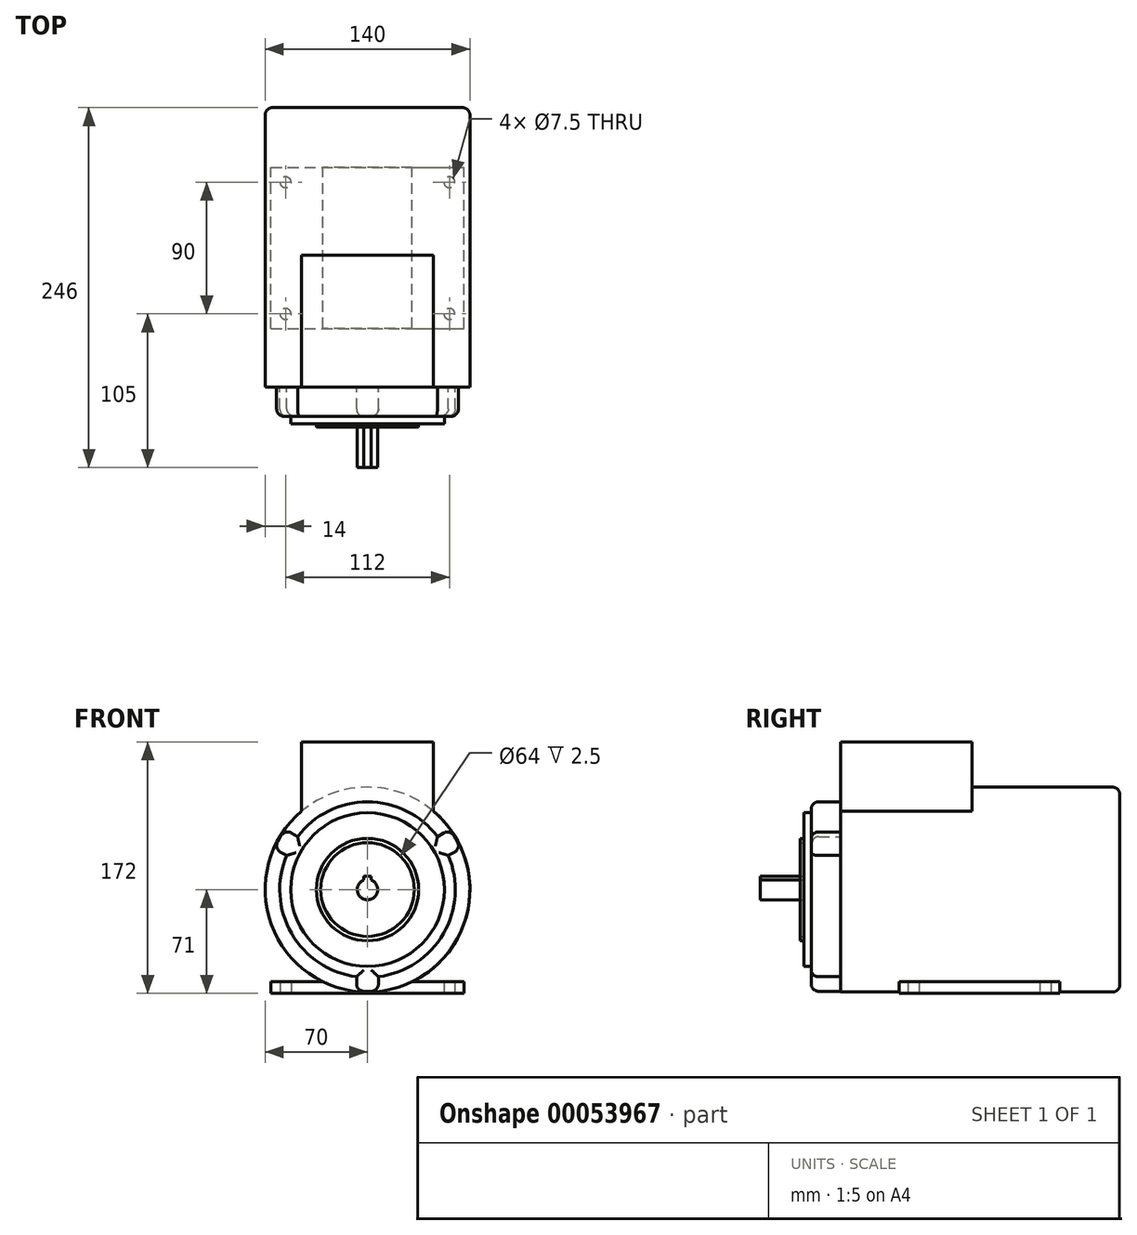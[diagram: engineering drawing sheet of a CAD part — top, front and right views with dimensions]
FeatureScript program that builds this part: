
annotation { "Feature Type Name" : "Feature", "Feature Type Description" : "" }
export const myFeature = defineFeature(function(context is Context, id is Id, definition is map)
    precondition{}
    {
        {
            var Q0;
            Q0=qCreatedBy(makeId("Front.planeOp"),FACE);
            var sketch = newSketch(context, id + "F0", { "sketchPlane" : qUnion([Q0])});
            skCircle(sketch, "E0", {"center": v(0, 0) * mm, "radius": 70 * mm});
            skSolve(sketch);
        }
        {
            var Q0;
            Q0 = qSketchRegion(id + "F0", true);
            extrude(context, id + "F1", {"entities" : qUnion([Q0]), "depth" : 191 * mm});
        }
        {
            var Q0;
            Q0=makeQuery(id+"F1.opExtrude","CAP_FACE",FACE,{"disambiguationData":[OSD([sQuery(id+"F0.wireOp",EDGE,"E0")])],"isStart":false});
            var sketch = newSketch(context, id + "F2", { "sketchPlane" : qUnion([Q0])});
            skCircle(sketch, "E1", {"center": v(0, 0) * mm, "radius": 60 * mm});
            skLineSegment(sketch, "E2.bottom", {"start": v(7.5, -59.53) * mm, "end": v(-7.5, -59.53) * mm});
            skLineSegment(sketch, "E2.top", {"start": v(7.5, -69.53) * mm, "end": v(-7.5, -69.53) * mm});
            skLineSegment(sketch, "E2.left", {"start": v(7.5, -59.53) * mm, "end": v(7.5, -69.53) * mm});
            skLineSegment(sketch, "E2.right", {"start": v(-7.5, -59.53) * mm, "end": v(-7.5, -69.53) * mm});
            skLineSegment(sketch, "E3", {"start": v(0, 0) * mm, "end": v(0, -69.53) * mm, "construction": true});
            skLineSegment(sketch, "E4.1.0", {"start": v(55.3, 23.27) * mm, "end": v(63.96, 28.27) * mm});
            skLineSegment(sketch, "E4.1.1", {"start": v(47.8, 36.26) * mm, "end": v(56.46, 41.26) * mm});
            skLineSegment(sketch, "E4.1.2", {"start": v(56.46, 41.26) * mm, "end": v(63.96, 28.27) * mm});
            skLineSegment(sketch, "E4.1.3", {"start": v(47.8, 36.26) * mm, "end": v(55.3, 23.27) * mm});
            skLineSegment(sketch, "E4.2.0", {"start": v(-47.8, 36.26) * mm, "end": v(-56.46, 41.26) * mm});
            skLineSegment(sketch, "E4.2.1", {"start": v(-55.3, 23.27) * mm, "end": v(-63.96, 28.27) * mm});
            skLineSegment(sketch, "E4.2.2", {"start": v(-63.96, 28.27) * mm, "end": v(-56.46, 41.26) * mm});
            skLineSegment(sketch, "E4.2.3", {"start": v(-55.3, 23.27) * mm, "end": v(-47.8, 36.26) * mm});
            skSolve(sketch);
        }
        {
            var Q0;
            Q0 = qSketchRegion(id + "F2", true);
            var Q1;
            Q1 = qConstructionFilter(qBodyType(qCreatedBy(id + "F2" ,EDGE), BodyType.WIRE), ConstructionObject.NO);
            extrude(context, id + "F3", {"entities" : qUnion([Q0]), "operationType" : NewBodyOperationType.ADD, "surfaceEntities" : qUnion([Q1]), "depth" : 20 * mm});
        }
        {
            var Q0;
            Q0=makeQuery(id+"F3.opExtrude","CAP_FACE",FACE,{"disambiguationData":[OSD([sQuery(id+"F2.wireOp",EDGE,"E1"),sQuery(id+"F2.wireOp",EDGE,"E2.top"),sQuery(id+"F2.wireOp",EDGE,"E2.left"),sQuery(id+"F2.wireOp",EDGE,"E2.right"),sQuery(id+"F2.wireOp",EDGE,"E4.1.0"),sQuery(id+"F2.wireOp",EDGE,"E4.1.1"),sQuery(id+"F2.wireOp",EDGE,"E4.1.2"),sQuery(id+"F2.wireOp",EDGE,"E4.2.0"),sQuery(id+"F2.wireOp",EDGE,"E4.2.1"),sQuery(id+"F2.wireOp",EDGE,"E4.2.2")])],"isStart":false});
            var sketch = newSketch(context, id + "F4", { "sketchPlane" : qUnion([Q0])});
            skCircle(sketch, "E5", {"center": v(0, 0) * mm, "radius": 52.5 * mm});
            skSolve(sketch);
        }
        {
            var Q0;
            Q0=makeQuery(id+"F4.imprint","IMPRINT",FACE,{"disambiguationData":[TD([[makeQuery(id+"F4.imprint","IMPRINT",EDGE,{"derivedFrom":sQuery(id+"F4.wireOp",EDGE,"E5")}),1.0]])]});
            extrude(context, id + "F5", {"entities" : qUnion([Q0]), "operationType" : NewBodyOperationType.ADD, "depth" : 5 * mm});
        }
        {
            var Q0;
            Q0=makeQuery(id+"F5.opExtrude","CAP_FACE",FACE,{"disambiguationData":[OSD([sQuery(id+"F4.wireOp",EDGE,"E5")])],"isStart":false});
            var sketch = newSketch(context, id + "F6", { "sketchPlane" : qUnion([Q0])});
            skCircle(sketch, "E6", {"center": v(0, 0) * mm, "radius": 35 * mm});
            skCircle(sketch, "E7", {"center": v(0, 0) * mm, "radius": 32 * mm});
            skSolve(sketch);
        }
        {
            var Q0;
            Q0=makeQuery(id+"F6.imprint","IMPRINT",FACE,{"disambiguationData":[TD([[makeQuery(id+"F6.imprint","IMPRINT",EDGE,{"derivedFrom":sQuery(id+"F6.wireOp",EDGE,"E6")}),1.0]])]});
            extrude(context, id + "F7", {"entities" : qUnion([Q0]), "operationType" : NewBodyOperationType.ADD, "depth" : 2.5 * mm});
        }
        {
            var Q0;
            Q0=makeQuery(id+"F7.boolean.opBoolean","SPLIT",FACE,{"disambiguationData":[TD([makeQuery(id+"F7.opExtrude","SWEPT_FACE",FACE,{"disambiguationData":[OSD([sQuery(id+"F6.wireOp",EDGE,"E7")])]})])],"derivedFrom":makeQuery(id+"F5.opExtrude","CAP_FACE",FACE,{"disambiguationData":[OSD([sQuery(id+"F4.wireOp",EDGE,"E5")])],"isStart":false})});
            var sketch = newSketch(context, id + "F8", { "sketchPlane" : qUnion([Q0])});
            skCircle(sketch, "E8", {"center": v(0, 0) * mm, "radius": 7 * mm});
            skLineSegment(sketch, "E9.bottom", {"start": v(2.5, 4) * mm, "end": v(-2.5, 4) * mm});
            skLineSegment(sketch, "E9.top", {"start": v(2.5, 9) * mm, "end": v(-2.5, 9) * mm});
            skLineSegment(sketch, "E9.left", {"start": v(2.5, 4) * mm, "end": v(2.5, 9) * mm});
            skLineSegment(sketch, "E9.right", {"start": v(-2.5, 4) * mm, "end": v(-2.5, 9) * mm});
            skLineSegment(sketch, "E10", {"start": v(0, 0) * mm, "end": v(0, 9) * mm, "construction": true});
            skPoint(sketch, "E11", {"position": v(0, -7) * mm});
            skSolve(sketch);
        }
        {
            var Q0;
            Q0 = qSketchRegion(id + "F8", true);
            extrude(context, id + "F9", {"entities" : qUnion([Q0]), "operationType" : NewBodyOperationType.ADD, "depth" : 30 * mm});
        }
        {
            var Q0;
            Q0=qCreatedBy(makeId("Top.planeOp"),FACE);
            var sketch = newSketch(context, id + "F10", { "sketchPlane" : qUnion([Q0])});
            skLineSegment(sketch, "E12.rect.bottom", {"start": v(-45, -191) * mm, "end": v(45, -191) * mm});
            skLineSegment(sketch, "E12.rect.top", {"start": v(-45, -101) * mm, "end": v(45, -101) * mm});
            skLineSegment(sketch, "E12.rect.left", {"start": v(-45, -191) * mm, "end": v(-45, -101) * mm});
            skLineSegment(sketch, "E12.rect.right", {"start": v(45, -191) * mm, "end": v(45, -101) * mm});
            skPoint(sketch, "E12.rect.middle", {"position": v(0, -146) * mm});
            skSolve(sketch);
        }
        {
            var Q0;
            Q0 = qSketchRegion(id + "F10", true);
            extrude(context, id + "F11", {"entities" : qUnion([Q0]), "operationType" : NewBodyOperationType.ADD, "depth" : 101 * mm});
        }
        {
            var Q0;
            Q0=qCreatedBy(makeId("Top.planeOp"),FACE);
            cPlane(context, id + "F12", {"entities" : qUnion([Q0]), "cplaneType" : CPlaneType.OFFSET, "offset" : 71 * mm, "oppositeDirection" : true, "width" : 150 * mm, "height" : 150 * mm});
        }
        {
            var Q0;
            Q0=qCreatedBy(id+"F12.planeOp",FACE);
            var sketch = newSketch(context, id + "F13", { "sketchPlane" : qUnion([Q0])});
            skLineSegment(sketch, "E13.rect.bottom", {"start": v(-66, -151) * mm, "end": v(66, -151) * mm});
            skLineSegment(sketch, "E13.rect.top", {"start": v(-66, -41) * mm, "end": v(66, -41) * mm});
            skLineSegment(sketch, "E13.rect.left", {"start": v(-66, -151) * mm, "end": v(-66, -41) * mm});
            skLineSegment(sketch, "E13.rect.right", {"start": v(66, -151) * mm, "end": v(66, -41) * mm});
            skPoint(sketch, "E13.rect.middle", {"position": v(0, -96) * mm});
            skPoint(sketch, "E14", {"position": v(56, -141) * mm});
            skLineSegment(sketch, "E15", {"start": v(0, -41) * mm, "end": v(0, -151) * mm, "construction": true});
            skLineSegment(sketch, "E16", {"start": v(66, -96) * mm, "end": v(-66, -96) * mm, "construction": true});
            skCircle(sketch, "E17", {"center": v(56, -141) * mm, "radius": 3.75 * mm});
            skCircle(sketch, "E18.MirrorC", {"center": v(56, -51) * mm, "radius": 3.75 * mm});
            skCircle(sketch, "E19.MirrorC", {"center": v(-56, -51) * mm, "radius": 3.75 * mm});
            skCircle(sketch, "E20.MirrorC", {"center": v(-56, -141) * mm, "radius": 3.75 * mm});
            skSolve(sketch);
        }
        {
            var Q0;
            Q0 = qSketchRegion(id + "F13", true);
            extrude(context, id + "F14", {"entities" : qUnion([Q0]), "operationType" : NewBodyOperationType.ADD, "depth" : 8 * mm});
        }
        {
            var Q0;
            Q0=makeQuery(id+"F1.opExtrude","CAP_EDGE",EDGE,{"disambiguationData":[OSD([sQuery(id+"F0.wireOp",EDGE,"E0")])],"isStart":true});
            var Q1;
            {var subQ0=sQuery(id+"F2.wireOp",EDGE,"E1");Q1=makeQuery(id+"F3.opExtrude","CAP_EDGE",EDGE,{"disambiguationData":[OSD([subQ0]),TDD([makeQuery(id+"F2.imprint","IMPRINT",EDGE,{"disambiguationData":[TD([[makeQuery(id+"F2.imprint","INTERSECT",VERTEX,{"derivedFrom":[subQ0,sQuery(id+"F2.wireOp",EDGE,"E4.1.1"),sQuery(id+"F2.wireOp",EDGE,"E4.1.3")]}),-1.0]])],"derivedFrom":subQ0})])],"isStart":false});}
            var Q2;
            Q2=makeQuery(id+"F3.opExtrude","CAP_EDGE",EDGE,{"disambiguationData":[OSD([sQuery(id+"F2.wireOp",EDGE,"E4.1.1")])],"isStart":false});
            var Q3;
            Q3=makeQuery(id+"F3.opExtrude","CAP_EDGE",EDGE,{"disambiguationData":[OSD([sQuery(id+"F2.wireOp",EDGE,"E4.1.0")])],"isStart":false});
            var Q4;
            {var subQ0=sQuery(id+"F2.wireOp",EDGE,"E1");Q4=makeQuery(id+"F3.opExtrude","CAP_EDGE",EDGE,{"disambiguationData":[OSD([subQ0]),TDD([makeQuery(id+"F2.imprint","IMPRINT",EDGE,{"disambiguationData":[TD([[makeQuery(id+"F2.imprint","INTERSECT",VERTEX,{"derivedFrom":[subQ0,sQuery(id+"F2.wireOp",EDGE,"E2.bottom"),sQuery(id+"F2.wireOp",EDGE,"E2.left")]}),-1.0]])],"derivedFrom":subQ0})])],"isStart":false});}
            var Q5;
            Q5=makeQuery(id+"F3.opExtrude","CAP_EDGE",EDGE,{"disambiguationData":[OSD([sQuery(id+"F2.wireOp",EDGE,"E2.left")])],"isStart":false});
            var Q6;
            Q6=makeQuery(id+"F3.opExtrude","CAP_EDGE",EDGE,{"disambiguationData":[OSD([sQuery(id+"F2.wireOp",EDGE,"E2.top")])],"isStart":false});
            var Q7;
            Q7=makeQuery(id+"F3.opExtrude","CAP_EDGE",EDGE,{"disambiguationData":[OSD([sQuery(id+"F2.wireOp",EDGE,"E2.right")])],"isStart":false});
            var Q8;
            {var subQ0=sQuery(id+"F2.wireOp",EDGE,"E1");Q8=makeQuery(id+"F3.opExtrude","CAP_EDGE",EDGE,{"disambiguationData":[OSD([subQ0]),TDD([makeQuery(id+"F2.imprint","IMPRINT",EDGE,{"disambiguationData":[TD([[makeQuery(id+"F2.imprint","INTERSECT",VERTEX,{"derivedFrom":[subQ0,sQuery(id+"F2.wireOp",EDGE,"E2.bottom"),sQuery(id+"F2.wireOp",EDGE,"E2.right")]}),1.0]])],"derivedFrom":subQ0})])],"isStart":false});}
            var Q9;
            Q9=makeQuery(id+"F3.opExtrude","CAP_EDGE",EDGE,{"disambiguationData":[OSD([sQuery(id+"F2.wireOp",EDGE,"E4.2.1")])],"isStart":false});
            var Q10;
            Q10=makeQuery(id+"F3.opExtrude","CAP_EDGE",EDGE,{"disambiguationData":[OSD([sQuery(id+"F2.wireOp",EDGE,"E4.2.2")])],"isStart":false});
            var Q11;
            Q11=makeQuery(id+"F3.opExtrude","CAP_EDGE",EDGE,{"disambiguationData":[OSD([sQuery(id+"F2.wireOp",EDGE,"E4.2.0")])],"isStart":false});
            var Q12;
            Q12=makeQuery(id+"F3.opExtrude","SWEPT_EDGE",EDGE,{"disambiguationData":[OSD([sQuery(id+"F2.wireOp",EDGE,"E4.2.0"),sQuery(id+"F2.wireOp",EDGE,"E4.2.2")])]});
            var Q13;
            Q13=makeQuery(id+"F3.opExtrude","SWEPT_EDGE",EDGE,{"disambiguationData":[OSD([sQuery(id+"F2.wireOp",EDGE,"E4.2.1"),sQuery(id+"F2.wireOp",EDGE,"E4.2.2")])]});
            var Q14;
            Q14=makeQuery(id+"F3.opExtrude","SWEPT_EDGE",EDGE,{"disambiguationData":[OSD([sQuery(id+"F2.wireOp",EDGE,"E4.1.1"),sQuery(id+"F2.wireOp",EDGE,"E4.1.2")])]});
            var Q15;
            Q15=makeQuery(id+"F3.opExtrude","SWEPT_EDGE",EDGE,{"disambiguationData":[OSD([sQuery(id+"F2.wireOp",EDGE,"E4.1.0"),sQuery(id+"F2.wireOp",EDGE,"E4.1.2")])]});
            var Q16;
            Q16=makeQuery(id+"F3.opExtrude","SWEPT_EDGE",EDGE,{"disambiguationData":[OSD([sQuery(id+"F2.wireOp",EDGE,"E2.top"),sQuery(id+"F2.wireOp",EDGE,"E2.left")])]});
            var Q17;
            Q17=makeQuery(id+"F3.opExtrude","SWEPT_EDGE",EDGE,{"disambiguationData":[OSD([sQuery(id+"F2.wireOp",EDGE,"E2.top"),sQuery(id+"F2.wireOp",EDGE,"E2.right")])]});
            var Q18;
            Q18=makeQuery(id+"F3.opExtrude","CAP_EDGE",EDGE,{"disambiguationData":[OSD([sQuery(id+"F2.wireOp",EDGE,"E4.1.2")])],"isStart":false});
            fillet(context, id + "F15", {"entities" : qUnion([Q0, Q1, Q2, Q3, Q4, Q5, Q6, Q7, Q8, Q9, Q10, Q11, Q12, Q13, Q14, Q15, Q16, Q17, Q18]), "radius" : 5 * mm, "tangentPropagation" : true, "allowEdgeOverflow" : false});
        }
    });
